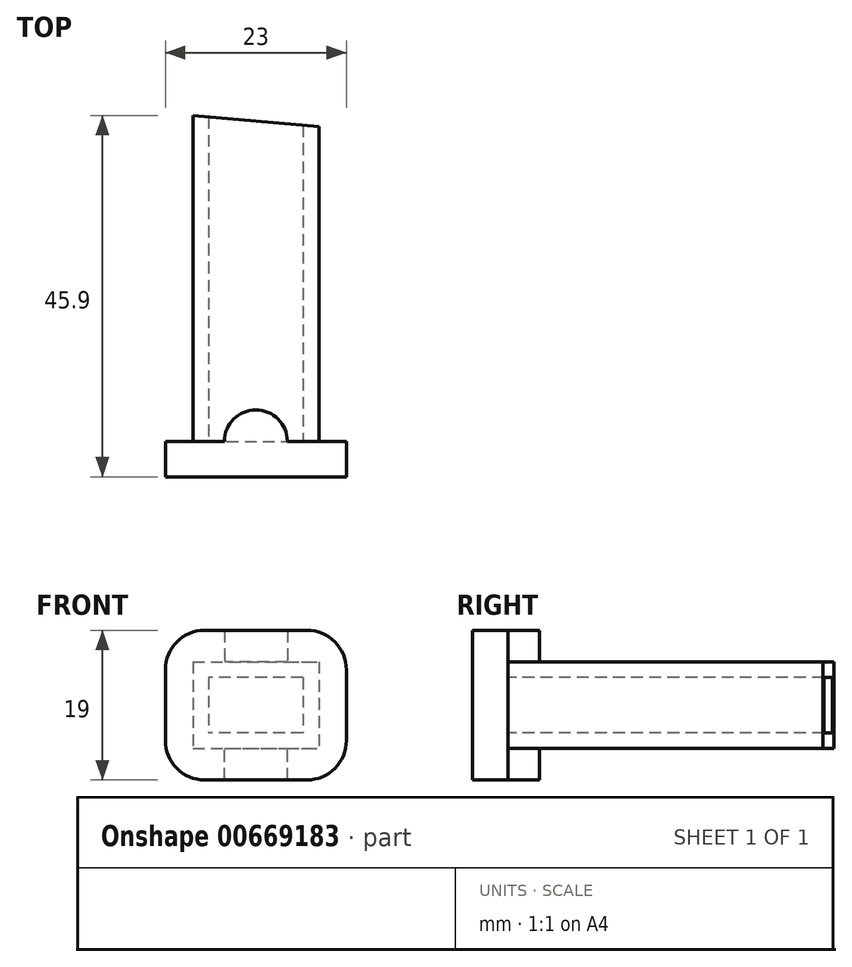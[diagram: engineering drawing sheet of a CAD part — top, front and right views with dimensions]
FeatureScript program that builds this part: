
annotation { "Feature Type Name" : "Feature", "Feature Type Description" : "" }
export const myFeature = defineFeature(function(context is Context, id is Id, definition is map)
    precondition{}
    {
        {
            var Q0;
            Q0=qCreatedBy(makeId("Top.planeOp"),FACE);
            var sketch = newSketch(context, id + "F0", { "sketchPlane" : qUnion([Q0])});
            skLineSegment(sketch, "E0", {"start": v(25.9, -9.84) * mm, "end": v(25.9, -51.24) * mm});
            skLineSegment(sketch, "E1", {"start": v(25.9, -9.84) * mm, "end": v(41.9, -11.24) * mm});
            skLineSegment(sketch, "E2", {"start": v(41.9, -11.24) * mm, "end": v(41.9, -51.24) * mm});
            skLineSegment(sketch, "E3", {"start": v(25.9, -51.24) * mm, "end": v(41.9, -51.24) * mm});
            skLineSegment(sketch, "E4", {"start": v(25.9, -51.24) * mm, "end": v(22.4, -51.24) * mm});
            skLineSegment(sketch, "E5", {"start": v(22.4, -51.24) * mm, "end": v(22.4, -55.74) * mm});
            skLineSegment(sketch, "E6", {"start": v(22.4, -55.74) * mm, "end": v(45.4, -55.74) * mm});
            skLineSegment(sketch, "E7", {"start": v(41.9, -51.24) * mm, "end": v(45.4, -51.24) * mm});
            skLineSegment(sketch, "E8", {"start": v(45.4, -51.24) * mm, "end": v(45.4, -55.74) * mm});
            skSolve(sketch);
        }
        {
            var Q0;
            {var subQ0=sQuery(id+"F0.wireOp",EDGE,"E2");Q0=makeQuery(id+"F0.imprint","IMPRINT",FACE,{"disambiguationData":[TD([[makeQuery(id+"F0.imprint","IMPRINT",EDGE,{"derivedFrom":subQ0}),-1.0]])]});}
            extrude(context, id + "F1", {"entities" : qUnion([Q0]), "endBound" : BoundingType.SYMMETRIC, "depth" : 11 * mm, "offsetDistance" : 25 * mm});
        }
        {
            var Q0;
            Q0=makeQuery(id+"F0.imprint","IMPRINT",FACE,{"disambiguationData":[TD([[makeQuery(id+"F0.imprint","IMPRINT",EDGE,{"derivedFrom":sQuery(id+"F0.wireOp",EDGE,"E3")}),-1.0]])]});
            var Q1;
            Q1=qSketchRegion(id+"F3",true);
            extrude(context, id + "F2", {"entities" : qUnion([Q0, Q1]), "operationType" : NewBodyOperationType.ADD, "endBound" : BoundingType.SYMMETRIC, "depth" : 19 * mm, "offsetDistance" : 25 * mm});
        }
        {
            var Q0;
            Q0=makeQuery(id+"F2.opExtrude","SWEPT_FACE",FACE,{"disambiguationData":[OSD([sQuery(id+"F0.wireOp",EDGE,"E3"),sQuery(id+"F0.wireOp",EDGE,"E4"),sQuery(id+"F0.wireOp",EDGE,"E7")])]});
            var sketch = newSketch(context, id + "F3", { "sketchPlane" : qUnion([Q0])});
            skLineSegment(sketch, "E9.bottom", {"start": v(-27.9, -3.5) * mm, "end": v(-39.9, -3.5) * mm});
            skLineSegment(sketch, "E9.top", {"start": v(-27.9, 3.5) * mm, "end": v(-39.9, 3.5) * mm});
            skLineSegment(sketch, "E9.left", {"start": v(-27.9, -3.5) * mm, "end": v(-27.9, 3.5) * mm});
            skLineSegment(sketch, "E9.right", {"start": v(-39.9, -3.5) * mm, "end": v(-39.9, 3.5) * mm});
            skSolve(sketch);
        }
        {
            var Q0;
            Q0=makeQuery(id+"F3.imprint","IMPRINT",FACE,{"disambiguationData":[TD([[makeQuery(id+"F3.imprint","IMPRINT",EDGE,{"derivedFrom":sQuery(id+"F3.wireOp",EDGE,"E9.bottom")}),-1.0]])]});
            extrude(context, id + "F4", {"entities" : qUnion([Q0]), "operationType" : NewBodyOperationType.REMOVE, "depth" : 44.1 * mm, "offsetDistance" : 25 * mm});
        }
        {
            var Q0;
            Q0=makeQuery(id+"F1.opExtrude","CAP_FACE",FACE,{"disambiguationData":[OSD([sQuery(id+"F0.wireOp",EDGE,"E0"),sQuery(id+"F0.wireOp",EDGE,"E1"),sQuery(id+"F0.wireOp",EDGE,"E2"),sQuery(id+"F0.wireOp",EDGE,"E3")])],"isStart":false});
            var sketch = newSketch(context, id + "F5", { "sketchPlane" : qUnion([Q0])});
            skCircle(sketch, "E10", {"center": v(33.9, -51.24) * mm, "radius": 4 * mm});
            skSolve(sketch);
        }
        {
            var Q0;
            {var subQ0=sQuery(id+"F5.wireOp",EDGE,"E10");var subQ1=makeQuery(id+"F1.opExtrude","CAP_EDGE",EDGE,{"disambiguationData":[OSD([sQuery(id+"F0.wireOp",EDGE,"E3")])],"isStart":false});var subQ2=makeQuery(id+"F5.imprint","INTERSECT",VERTEX,{"disambiguationData":[OD(0.0)],"derivedFrom":[subQ1,subQ0]});Q0=makeQuery(id+"F5.imprint","IMPRINT",FACE,{"disambiguationData":[TD([[makeQuery(id+"F5.imprint","IMPRINT",EDGE,{"disambiguationData":[TD([[subQ2,1.0]])],"derivedFrom":subQ0}),1.0]])]});}
            extrude(context, id + "F6", {"entities" : qUnion([Q0]), "operationType" : NewBodyOperationType.ADD, "depth" : 4 * mm, "offsetDistance" : 25 * mm});
        }
        {
            var Q0;
            Q0=makeQuery(id+"F1.opExtrude","CAP_FACE",FACE,{"disambiguationData":[OSD([sQuery(id+"F0.wireOp",EDGE,"E0"),sQuery(id+"F0.wireOp",EDGE,"E1"),sQuery(id+"F0.wireOp",EDGE,"E2"),sQuery(id+"F0.wireOp",EDGE,"E3")])],"isStart":true});
            var sketch = newSketch(context, id + "F7", { "sketchPlane" : qUnion([Q0])});
            skCircle(sketch, "E11", {"center": v(33.9, 51.24) * mm, "radius": 4 * mm});
            skSolve(sketch);
        }
        {
            var Q0;
            {var subQ0=sQuery(id+"F7.wireOp",EDGE,"E11");var subQ1=makeQuery(id+"F1.opExtrude","CAP_EDGE",EDGE,{"disambiguationData":[OSD([sQuery(id+"F0.wireOp",EDGE,"E3")])],"isStart":true});var subQ2=makeQuery(id+"F7.imprint","INTERSECT",VERTEX,{"disambiguationData":[OD(0.0)],"derivedFrom":[subQ1,subQ0]});Q0=makeQuery(id+"F7.imprint","IMPRINT",FACE,{"disambiguationData":[TD([[makeQuery(id+"F7.imprint","IMPRINT",EDGE,{"disambiguationData":[TD([[subQ2,-1.0]])],"derivedFrom":subQ0}),1.0]])]});}
            extrude(context, id + "F8", {"entities" : qUnion([Q0]), "operationType" : NewBodyOperationType.ADD, "depth" : 4 * mm, "offsetDistance" : 25 * mm});
        }
        {
            var Q0;
            Q0=makeQuery(id+"F2.opExtrude","CAP_EDGE",EDGE,{"disambiguationData":[OSD([sQuery(id+"F0.wireOp",EDGE,"E5")])],"isStart":false});
            fillet(context, id + "F9", {"entities" : qUnion([Q0]), "radius" : 5 * mm, "tangentPropagation" : true, "allowEdgeOverflow" : false});
        }
        {
            var Q0;
            Q0=makeQuery(id+"F2.opExtrude","CAP_EDGE",EDGE,{"disambiguationData":[OSD([sQuery(id+"F0.wireOp",EDGE,"E8")])],"isStart":false});
            fillet(context, id + "F10", {"entities" : qUnion([Q0]), "radius" : 5 * mm, "tangentPropagation" : true, "allowEdgeOverflow" : false});
        }
        {
            var Q0;
            Q0=makeQuery(id+"F2.opExtrude","CAP_EDGE",EDGE,{"disambiguationData":[OSD([sQuery(id+"F0.wireOp",EDGE,"E8")])],"isStart":true});
            fillet(context, id + "F11", {"entities" : qUnion([Q0]), "radius" : 5 * mm, "tangentPropagation" : true, "allowEdgeOverflow" : false});
        }
        {
            var Q0;
            Q0=makeQuery(id+"F2.opExtrude","CAP_EDGE",EDGE,{"disambiguationData":[OSD([sQuery(id+"F0.wireOp",EDGE,"E5")])],"isStart":true});
            fillet(context, id + "F12", {"entities" : qUnion([Q0]), "radius" : 5 * mm, "tangentPropagation" : true, "allowEdgeOverflow" : false});
        }
    });
